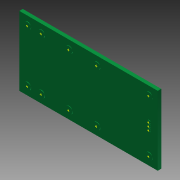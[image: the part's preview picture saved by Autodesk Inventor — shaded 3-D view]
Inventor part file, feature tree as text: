
AUTODESK INVENTOR PART (.ipt)
format: ipt  version: 2011 SP1 (Build 150282100, 282)  size: 141,312 bytes
history: native  units: in
note: dims shown in document units (in); Inventor stores cm internally (conversion verified against a paired STEP export)
features: sketch x15, other x6, extrude x2
ambient origin geometry x8: Origin, YZ Plane, XZ Plane, XY Plane, X Axis, Y Axis, Z Axis, Center Point
bodies: Solid1 (feature_tree)
feature tree (23):
  extrude  "Extrusion1"  Depth=2.5in
  extrude  "Extrusion2"  Depth=0.1527in
  sketch  "Sketch3"  dims[d5=0.1527in]
  sketch  "Sketch4"  dims[d6=0.1527in]
  sketch  "Sketch5"  dims[d7=0.125in]
  sketch  "Sketch6"  dims[d8=0.0625in]
  sketch  "Sketch7"  dims[d9=0.125in d10=0.1527in]
  sketch  "Sketch8"  dims[d11=0.1527in]
  sketch  "Sketch9"  dims[d12=0.7874in d14=0.25in d15=0.3937in d17=1.0in]
  other  "L7.4+"
  sketch  "Sketch10"  dims[d19=0.7874in d21=0.5in d22=0.3937in d24=1.0in]
  other  "L7.4-"
  sketch  "Sketch11"  dims[d26=0.7874in d28=0.5in d29=0.3937in d31=1.0in]
  other  "T7.4+"
  sketch  "Sketch12"  dims[d33=0.01in d34=0.0in]
  other  "T7.4-"
  sketch  "Sketch13"
  other  "S2-"
  sketch  "Sketch14"
  other  "S1-"
  sketch  "Sketch15"
  sketch  "Sketch1"  dims[d0=1.25in d1=2.5in]
  sketch  "Sketch2"  dims[d2=0.0625in d3=0.0in d4=0.1527in]
